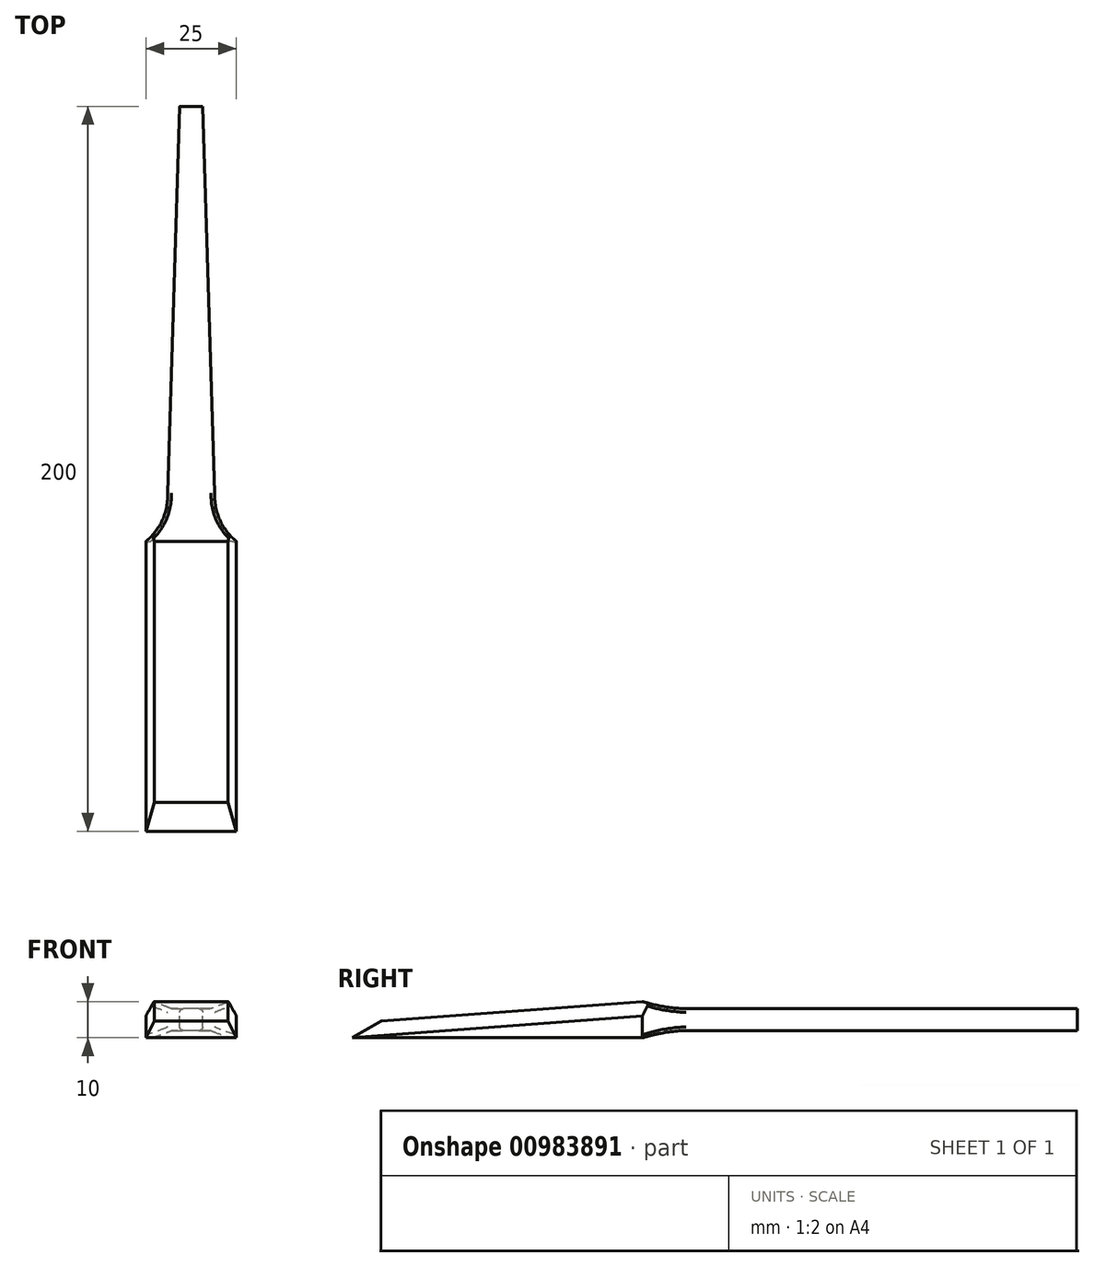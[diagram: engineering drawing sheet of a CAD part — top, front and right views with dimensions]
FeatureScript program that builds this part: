
annotation { "Feature Type Name" : "Feature", "Feature Type Description" : "" }
export const myFeature = defineFeature(function(context is Context, id is Id, definition is map)
    precondition{}
    {
        {
            var Q0;
            Q0=qCreatedBy(makeId("Right.planeOp"),FACE);
            var sketch = newSketch(context, id + "F0", { "sketchPlane" : qUnion([Q0])});
            skLineSegment(sketch, "E0", {"start": v(0, 0) * mm, "end": v(-80, 0) * mm});
            skLineSegment(sketch, "E1", {"start": v(0, 0) * mm, "end": v(0, 10) * mm});
            skLineSegment(sketch, "E2", {"start": v(-72.04, 4.6) * mm, "end": v(0, 10) * mm});
            skLineSegment(sketch, "E3", {"start": v(-80, 0) * mm, "end": v(-72.04, 4.6) * mm});
            skLineSegment(sketch, "E4", {"start": v(0, 10) * mm, "end": v(120, 10) * mm});
            skLineSegment(sketch, "E5", {"start": v(120, 10) * mm, "end": v(120, 0) * mm});
            skLineSegment(sketch, "E6", {"start": v(120, 0) * mm, "end": v(0, 0) * mm});
            skSolve(sketch);
        }
        {
            var Q0;
            Q0 = qSketchRegion(id + "F0", true);
            extrude(context, id + "F1", {"entities" : qUnion([Q0]), "depth" : 25 * mm, "offsetDistance" : 25 * mm});
        }
        {
            var Q0;
            Q0=makeQuery(id+"F1.opExtrude","SWEPT_FACE",FACE,{"disambiguationData":[OSD([sQuery(id+"F0.wireOp",EDGE,"E4")])]});
            var sketch = newSketch(context, id + "F2", { "sketchPlane" : qUnion([Q0])});
            skArc(sketch, "E7", {"start": v(19, 12) * mm, "mid": v(20.68, 5.34) * mm, "end": v(25, 0) * mm});
            skArc(sketch, "E8", {"start": v(0, 0) * mm, "mid": v(4.32, 5.34) * mm, "end": v(6, 12) * mm});
            skLineSegment(sketch, "E9", {"start": v(9.35, 120) * mm, "end": v(6, 12) * mm});
            skLineSegment(sketch, "E10", {"start": v(19, 12) * mm, "end": v(15.65, 120) * mm});
            skLineSegment(sketch, "E11", {"start": v(9.35, 120) * mm, "end": v(15.65, 120) * mm});
            skSolve(sketch);
        }
        {
            var Q0;
            Q0 = qSketchRegion(id + "F2", true);
            var Q1;
            Q1=makeQuery(id+"F2.imprint","IMPRINT",FACE,{"disambiguationData":[TD([[makeQuery(id+"F2.imprint","IMPRINT",EDGE,{"derivedFrom":sQuery(id+"F2.wireOp",EDGE,"E8")}),1.0]])]});
            var Q2;
            Q2=makeQuery(id+"F2.imprint","IMPRINT",FACE,{"disambiguationData":[TD([[makeQuery(id+"F2.imprint","IMPRINT",EDGE,{"derivedFrom":sQuery(id+"F2.wireOp",EDGE,"E7")}),1.0]])]});
            extrude(context, id + "F3", {"entities" : qUnion([Q0, Q1, Q2]), "operationType" : NewBodyOperationType.REMOVE, "oppositeDirection" : true, "depth" : 25 * mm, "offsetDistance" : 25 * mm});
        }
        {
            var Q0;
            Q0=qCreatedBy(makeId("Right.planeOp"),FACE);
            var sketch = newSketch(context, id + "F4", { "sketchPlane" : qUnion([Q0])});
            skArc(sketch, "E12", {"start": v(13.27, 2) * mm, "mid": v(6.56, 1.5) * mm, "end": v(0, 0) * mm});
            skLineSegment(sketch, "E13", {"start": v(13.27, 2) * mm, "end": v(120, 2) * mm});
            skLineSegment(sketch, "E14", {"start": v(0, 0) * mm, "end": v(0, 5) * mm});
            skLineSegment(sketch, "E15.MirrorCS", {"start": v(13.27, 8) * mm, "end": v(120, 8) * mm});
            skArc(sketch, "E16.MirrorCS", {"start": v(13.27, 8) * mm, "mid": v(6.56, 8.5) * mm, "end": v(0, 10) * mm});
            skLineSegment(sketch, "E17", {"start": v(120, 2) * mm, "end": v(120, 8) * mm});
            skLineSegment(sketch, "E18", {"start": v(0, 10) * mm, "end": v(0, 5) * mm});
            skLineSegment(sketch, "E19", {"start": v(0, 10) * mm, "end": v(120, 10) * mm});
            skLineSegment(sketch, "E20", {"start": v(120, 10) * mm, "end": v(120, 8) * mm});
            skLineSegment(sketch, "E21", {"start": v(120, 2) * mm, "end": v(120, 0) * mm});
            skLineSegment(sketch, "E22", {"start": v(120, 0) * mm, "end": v(0, 0) * mm});
            skSolve(sketch);
        }
        {
            var Q0;
            Q0=makeQuery(id+"F4.imprint","IMPRINT",FACE,{"disambiguationData":[TD([[makeQuery(id+"F4.imprint","IMPRINT",EDGE,{"derivedFrom":sQuery(id+"F4.wireOp",EDGE,"E12")}),1.0]])]});
            var Q1;
            Q1=makeQuery(id+"F4.imprint","IMPRINT",FACE,{"disambiguationData":[TD([[makeQuery(id+"F4.imprint","IMPRINT",EDGE,{"derivedFrom":sQuery(id+"F4.wireOp",EDGE,"E15.MirrorCS")}),1.0]])]});
            extrude(context, id + "F5", {"entities" : qUnion([Q0, Q1]), "operationType" : NewBodyOperationType.REMOVE, "depth" : 25 * mm, "offsetDistance" : 25 * mm});
        }
        {
            var Q0;
            Q0=makeQuery(id+"F5.boolean.opBoolean","INTERSECT",EDGE,{"derivedFrom":[makeQuery(id+"F3.boolean.opBoolean","COPY",FACE,{"derivedFrom":makeQuery(id+"F3.opExtrude","SWEPT_FACE",FACE,{"disambiguationData":[OSD([sQuery(id+"F2.wireOp",EDGE,"E9")])]})}),makeQuery(id+"F5.opExtrude","SWEPT_FACE",FACE,{"disambiguationData":[OSD([sQuery(id+"F4.wireOp",EDGE,"E15.MirrorCS")])]})]});
            var Q1;
            Q1=makeQuery(id+"F5.boolean.opBoolean","INTERSECT",EDGE,{"derivedFrom":[makeQuery(id+"F3.boolean.opBoolean","COPY",FACE,{"derivedFrom":makeQuery(id+"F3.opExtrude","SWEPT_FACE",FACE,{"disambiguationData":[OSD([sQuery(id+"F2.wireOp",EDGE,"E10")])]})}),makeQuery(id+"F5.opExtrude","SWEPT_FACE",FACE,{"disambiguationData":[OSD([sQuery(id+"F4.wireOp",EDGE,"E15.MirrorCS")])]})]});
            var Q2;
            Q2=makeQuery(id+"F5.boolean.opBoolean","INTERSECT",EDGE,{"derivedFrom":[makeQuery(id+"F3.boolean.opBoolean","COPY",FACE,{"derivedFrom":makeQuery(id+"F3.opExtrude","SWEPT_FACE",FACE,{"disambiguationData":[OSD([sQuery(id+"F2.wireOp",EDGE,"E10")])]})}),makeQuery(id+"F5.opExtrude","SWEPT_FACE",FACE,{"disambiguationData":[OSD([sQuery(id+"F4.wireOp",EDGE,"E13")])]})]});
            var Q3;
            Q3=makeQuery(id+"F5.boolean.opBoolean","INTERSECT",EDGE,{"derivedFrom":[makeQuery(id+"F3.boolean.opBoolean","COPY",FACE,{"derivedFrom":makeQuery(id+"F3.opExtrude","SWEPT_FACE",FACE,{"disambiguationData":[OSD([sQuery(id+"F2.wireOp",EDGE,"E9")])]})}),makeQuery(id+"F5.opExtrude","SWEPT_FACE",FACE,{"disambiguationData":[OSD([sQuery(id+"F4.wireOp",EDGE,"E13")])]})]});
            fillet(context, id + "F6", {"entities" : qUnion([Q0, Q1, Q2, Q3]), "radius" : 1 * mm, "tangentPropagation" : true, "allowEdgeOverflow" : false});
        }
        {
            var Q0;
            Q0=makeQuery(id+"F1.opExtrude","CAP_EDGE",EDGE,{"disambiguationData":[OSD([sQuery(id+"F0.wireOp",EDGE,"E2")])],"isStart":true});
            var Q1;
            Q1=makeQuery(id+"F1.opExtrude","CAP_EDGE",EDGE,{"disambiguationData":[OSD([sQuery(id+"F0.wireOp",EDGE,"E2")])],"isStart":false});
            chamfer(context, id + "F7", {"entities" : qUnion([Q0, Q1]), "chamferType" : ChamferType.OFFSET_ANGLE, "width" : 4 * mm, "oppositeDirection" : false, "angle" : 30 * degree, "tangentPropagation" : true});
        }
    });
